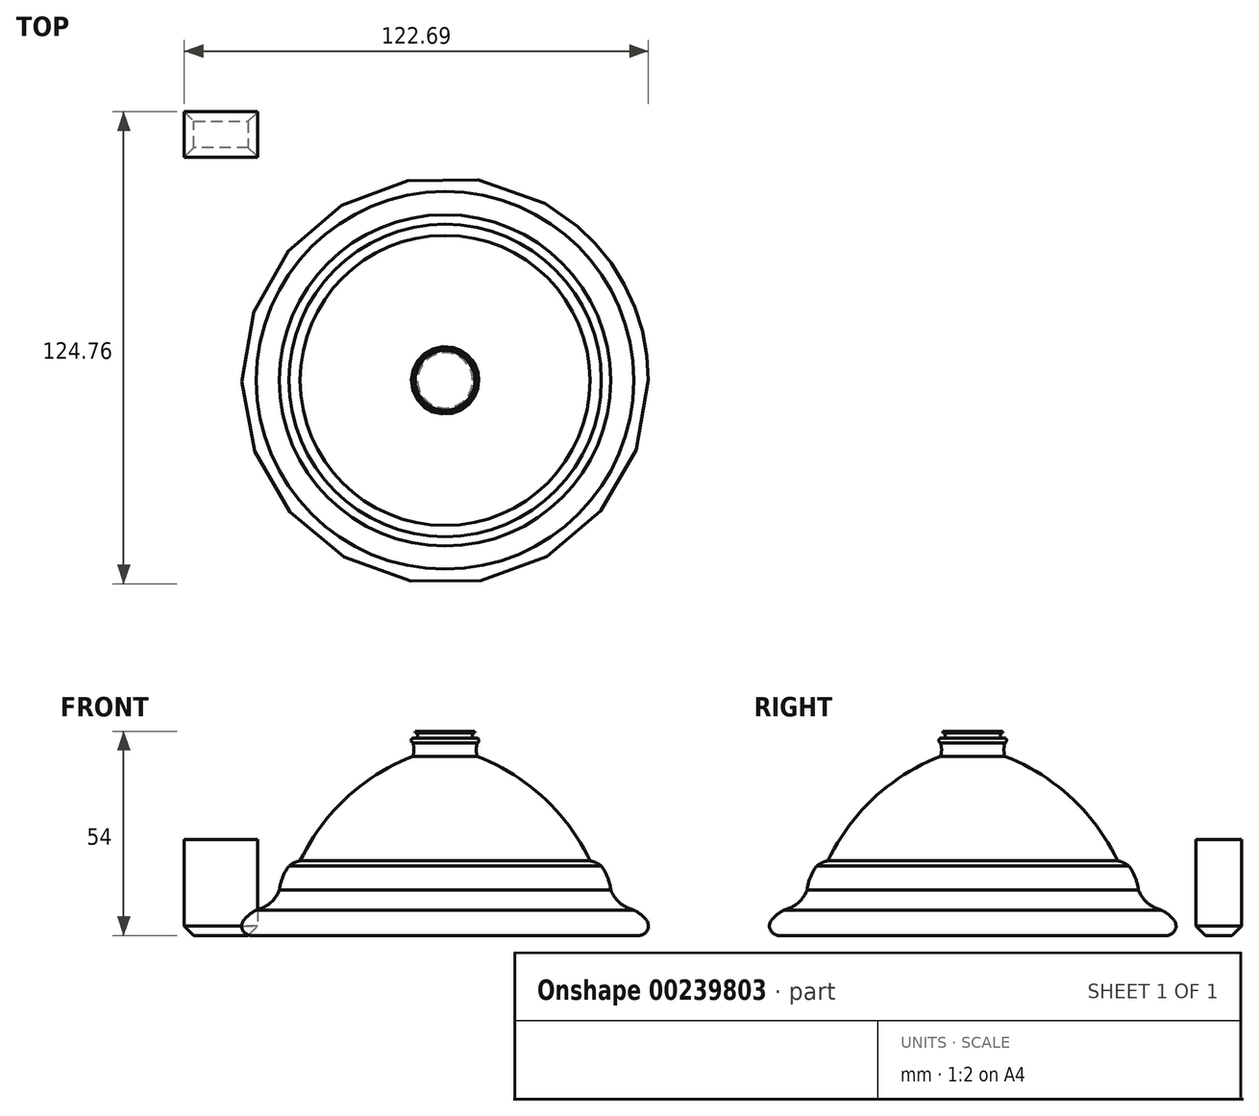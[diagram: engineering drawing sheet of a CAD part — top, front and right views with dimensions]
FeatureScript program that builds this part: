
annotation { "Feature Type Name" : "Feature", "Feature Type Description" : "" }
export const myFeature = defineFeature(function(context is Context, id is Id, definition is map)
    precondition{}
    {
        {
            var Q0;
            Q0=qCreatedBy(makeId("Front.planeOp"),FACE);
            var sketch = newSketch(context, id + "F0", { "sketchPlane" : qUnion([Q0])});
            skLineSegment(sketch, "E0", {"start": v(0, 0) * mm, "end": v(-55.21, 0) * mm});
            skArc(sketch, "E1", {"start": v(-49.9, 6.7) * mm, "mid": v(-53.32, 3.96) * mm, "end": v(-55.21, 0) * mm});
            skArc(sketch, "E2", {"start": v(-49.9, 6.7) * mm, "mid": v(-46.2, 8.64) * mm, "end": v(-43.79, 12.05) * mm});
            skArc(sketch, "E3", {"start": v(-41.29, 18.35) * mm, "mid": v(-42.96, 15.37) * mm, "end": v(-43.79, 12.05) * mm});
            skArc(sketch, "E4", {"start": v(-38.32, 19.74) * mm, "mid": v(-39.9, 19.26) * mm, "end": v(-41.29, 18.35) * mm});
            skArc(sketch, "E5", {"start": v(-8.51, 47.34) * mm, "mid": v(-26.07, 36.4) * mm, "end": v(-38.32, 19.74) * mm});
            skArc(sketch, "E6", {"start": v(-8.51, 47.34) * mm, "mid": v(-8.24, 49.12) * mm, "end": v(-8.51, 50.9) * mm});
            skArc(sketch, "E7", {"start": v(-8.51, 52.22) * mm, "mid": v(-8.92, 51.56) * mm, "end": v(-8.51, 50.9) * mm});
            skLineSegment(sketch, "E8", {"start": v(-8.51, 52.22) * mm, "end": v(-7.27, 52.22) * mm});
            skLineSegment(sketch, "E9", {"start": v(-7.27, 52.22) * mm, "end": v(-7.27, 53.57) * mm});
            skLineSegment(sketch, "E10", {"start": v(-7.27, 53.57) * mm, "end": v(-7.9, 53.57) * mm});
            skLineSegment(sketch, "E11", {"start": v(-7.9, 53.57) * mm, "end": v(-7.9, 54) * mm});
            skLineSegment(sketch, "E12", {"start": v(-7.9, 54) * mm, "end": v(0, 54) * mm});
            skLineSegment(sketch, "E13", {"start": v(0, 54) * mm, "end": v(0, 0) * mm});
            skSolve(sketch);
        }
        {
            var Q0;
            Q0=makeQuery(id+"F0.imprint","IMPRINT",FACE,{"disambiguationData":[TD([[makeQuery(id+"F0.imprint","IMPRINT",EDGE,{"derivedFrom":sQuery(id+"F0.wireOp",EDGE,"E0")}),-1.0]])]});
            var Q1;
            Q1=sQuery(id+"F0.wireOp",EDGE,"E13");
            revolve(context, id + "F1", {"entities" : qUnion([Q0]), "axis" : qUnion([Q1]), "revolveType" : RevolveType.FULL});
        }
        {
            var Q0;
            Q0=qCreatedBy(makeId("Top.planeOp"),FACE);
            var sketch = newSketch(context, id + "F2", { "sketchPlane" : qUnion([Q0])});
            skLineSegment(sketch, "E14.bottom", {"start": v(-68.95, 71.02) * mm, "end": v(-49.5, 71.02) * mm});
            skLineSegment(sketch, "E14.top", {"start": v(-68.95, 59.03) * mm, "end": v(-49.5, 59.03) * mm});
            skLineSegment(sketch, "E14.left", {"start": v(-68.95, 71.02) * mm, "end": v(-68.95, 59.03) * mm});
            skLineSegment(sketch, "E14.right", {"start": v(-49.5, 71.02) * mm, "end": v(-49.5, 59.03) * mm});
            skSolve(sketch);
        }
        {
            var Q0;
            Q0 = qSketchRegion(id + "F2", true);
            extrude(context, id + "F3", {"entities" : qUnion([Q0]), "depth" : 25.4 * mm});
        }
        {
            var Q0;
            Q0=makeQuery(id+"F1.opRevolve","SWEPT_EDGE",EDGE,{"disambiguationData":[OSD([sQuery(id+"F0.wireOp",EDGE,"E0"),sQuery(id+"F0.wireOp",EDGE,"E1")])]});
            fillet(context, id + "F4", {"entities" : qUnion([Q0]), "radius" : 2.54 * mm, "tangentPropagation" : true, "allowEdgeOverflow" : false});
        }
        {
            var Q0;
            Q0=makeQuery(id+"F3.opExtrude","CAP_FACE",FACE,{"disambiguationData":[OSD([sQuery(id+"F2.wireOp",EDGE,"E14.bottom"),sQuery(id+"F2.wireOp",EDGE,"E14.top"),sQuery(id+"F2.wireOp",EDGE,"E14.left"),sQuery(id+"F2.wireOp",EDGE,"E14.right")])],"isStart":true});
            chamfer(context, id + "F5", {"entities" : qUnion([Q0]), "width" : 2.54 * mm, "tangentPropagation" : true});
        }
    });
